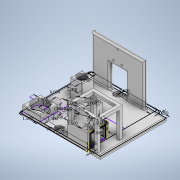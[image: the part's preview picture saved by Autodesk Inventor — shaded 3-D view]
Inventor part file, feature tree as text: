
AUTODESK INVENTOR PART (.ipt)
format: ipt  version: 2020 (Build 240168000, 168)  size: 1,240,576 bytes
history: native  units: in
note: dims shown in document units (in); Inventor stores cm internally (conversion verified against a paired STEP export)
features: extrude x18, sketch x12, fillet x7, hole x2
ambient origin geometry x8: Origin, YZ Plane, XZ Plane, XY Plane, X Axis, Y Axis, Z Axis, Center Point
bodies: Solid1 (feature_tree)
feature tree (39):
  sketch  "Sketch1"  dims[d0=5.6in d1=6.0in]
  extrude  "Extrusion1"  Depth=6.0in
  hole  "Hole1"  [1 undecoded]
  extrude  "Extrusion2"  Depth=5.6in
  extrude  "Extrusion3"  Depth=5.6in
  extrude  "Extrusion4"  Depth=0.25in TaperAngle=0.0deg
  extrude  "Extrusion5"  Depth=1.0in
  extrude  "Extrusion6"  Depth=1.5in
  hole  "Hole2"  [1 undecoded]
  extrude  "Extrusion7"  TaperAngle=180.0deg  [1 undecoded]
  extrude  "Extrusion8"  Depth=1.5in
  extrude  "Extrusion9"  Depth=1.5in
  sketch  "Sketch6"  dims[d11=0.266in d12=0.75in d13=0.625in d14=0.19in d15=0.5635in d16=1.0in d17=0.8108in d18=1.5in]
  extrude  "Extrusion10"  Depth=2.5in
  sketch  "Sketch7"  dims[d19=0.6in d20=1.5in]
  extrude  "Extrusion11"  Depth=2.5in TaperAngle=0.0deg
  extrude  "Extrusion12"  Depth=2.5in TaperAngle=0.0deg
  extrude  "Extrusion13"  Depth=1.0in TaperAngle=0.0deg
  fillet  "Fillet1"  Radius=1.5in
  fillet  "Fillet2"  Radius=0.325in
  fillet  "Fillet3"  Radius=2.0in
  fillet  "Fillet4"  Radius=1.5in
  fillet  "Fillet5"  Radius=0.333in
  fillet  "Fillet6"  Radius=0.96in
  fillet  "Fillet7"  Radius=0.356in
  sketch  "Sketch8"  dims[d21=1.5in d22=0.6in]
  sketch  "Sketch9"  dims[d23=1.5in d24=180.0deg]
  extrude  "Extrusion14"  Depth=2.5in
  extrude  "Extrusion15"  Depth=2.5in
  extrude  "Extrusion16"  Depth=1.0in
  extrude  "Extrusion17"  Depth=1.0in
  extrude  "Extrusion18"  Depth=1.0in
  sketch  "Sketch2"  dims[d2=0.5in d3=90.0deg]
  sketch  "Sketch3"  dims[d4=0.5in d5=5.6in]
  sketch  "Sketch4"  dims[d6=0.2in d7=5.6in]
  sketch  "Sketch5"  dims[d8=0.2in d9=0.25in d10=0.0in]
  sketch  "Sketch10"  dims[d25=1.5in d26=1.5in]
  sketch  "Sketch11"  dims[d27=1.5in d28=1.5in]
  sketch  "Sketch12"  dims[d29=1.3in d30=1.3in d31=0.5in d32=0.0in d33=0.5in d34=0.0in d35=1.0in d36=0.0in d37=1.5in d38=0.325in d39=2.0in d40=0.0in d41=1.5in d42=0.0in d43=0.333in d44=0.96in d45=0.356in d46=0.356in d47=0.134in d48=0.75in d49=0.256in d50=0.118in d51=90.0deg d52=1.0in d53=0.8108in d54=1.75in d55=1.0in d56=1.0in d57=1.0in d58=0.78in d59=1.5in d60=0.0in d61=0.25in d62=0.25in d63=1.5in d64=0.0in d65=1.25in d66=0.0in d67=0.125in d68=0.125in d69=0.125in d70=0.125in d71=1.725in d72=0.0in d73=0.25in d74=0.25in d75=1.043in d76=0.748in d77=0.25in d78=0.0in d79=0.25in d80=0.25in d81=0.0625in d82=0.0625in d83=0.0625in d84=0.0625in d85=0.1875in d86=0.0in d87=0.125in d88=0.0in d89=0.125in d90=0.125in d91=0.0625in d92=0.0625in d93=0.0625in d94=0.0625in d95=0.0625in d96=0.0197in d97=0.0in d98=0.0197in d99=0.0in d100=1.0in d101=0.25in d102=0.25in d103=1.614in d104=90.0deg d105=1.969in d106=0.0in d107=0.25in d108=0.25in d109=0.25in d110=0.25in d111=0.25in d112=0.25in d113=2.5in d114=0.0in d115=0.25in d116=0.25in d117=0.25in d118=0.25in d119=2.5in d120=0.0in d121=2.5in d122=0.0in]
note: 3 required parameter values undecoded (feature->parameter linkage not recoverable at this tier; creation-order binding heuristic only, values carry confidence <= 0.55)
